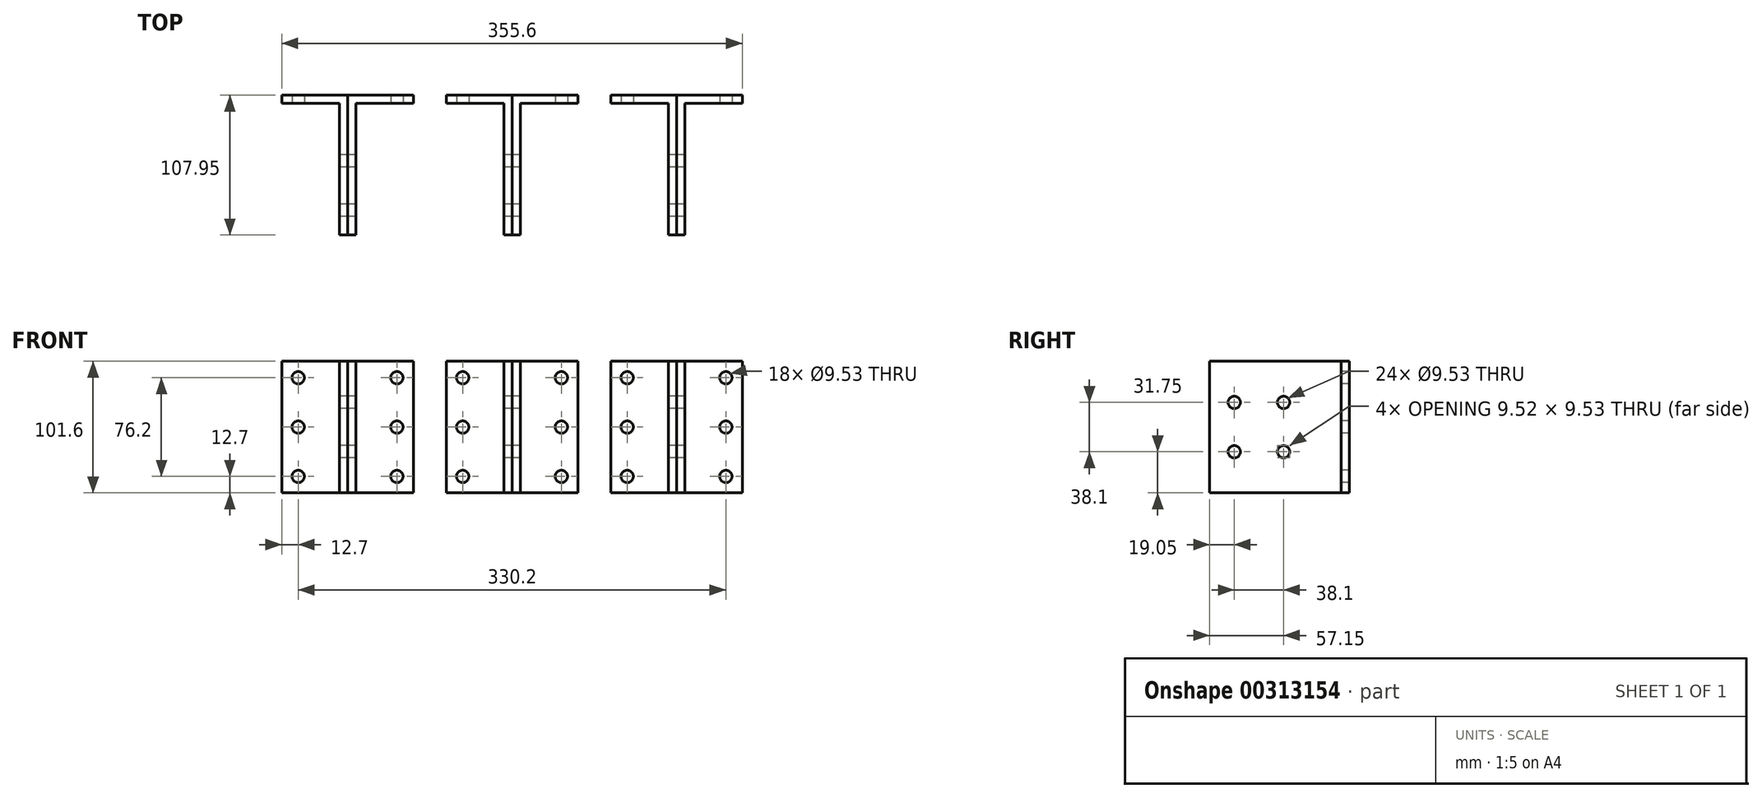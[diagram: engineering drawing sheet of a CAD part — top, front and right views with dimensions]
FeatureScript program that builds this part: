
annotation { "Feature Type Name" : "Feature", "Feature Type Description" : "" }
export const myFeature = defineFeature(function(context is Context, id is Id, definition is map)
    precondition{}
    {
        {
            var Q0;
            Q0=qCreatedBy(makeId("Top.planeOp"),FACE);
            var sketch = newSketch(context, id + "F0", { "sketchPlane" : qUnion([Q0])});
            skLineSegment(sketch, "E0", {"start": v(-44.45, 0) * mm, "end": v(0, 0) * mm});
            skLineSegment(sketch, "E1", {"start": v(0, 0) * mm, "end": v(0, -101.6) * mm});
            skLineSegment(sketch, "E2", {"start": v(0, -101.6) * mm, "end": v(6.35, -101.6) * mm});
            skLineSegment(sketch, "E3", {"start": v(6.35, -101.6) * mm, "end": v(6.35, 6.35) * mm});
            skLineSegment(sketch, "E4", {"start": v(6.35, 6.35) * mm, "end": v(-44.45, 6.35) * mm});
            skLineSegment(sketch, "E5", {"start": v(-44.45, 6.35) * mm, "end": v(-44.45, 0) * mm});
            skLineSegment(sketch, "E6.1.0.0", {"start": v(82.55, 0) * mm, "end": v(127, 0) * mm});
            skLineSegment(sketch, "E6.1.0.1", {"start": v(127, 0) * mm, "end": v(127, -101.6) * mm});
            skLineSegment(sketch, "E6.1.0.2", {"start": v(133.35, -101.6) * mm, "end": v(133.35, 6.35) * mm});
            skLineSegment(sketch, "E6.1.0.3", {"start": v(133.35, 6.35) * mm, "end": v(82.55, 6.35) * mm});
            skLineSegment(sketch, "E6.1.0.4", {"start": v(127, -101.6) * mm, "end": v(133.35, -101.6) * mm});
            skLineSegment(sketch, "E6.1.0.5", {"start": v(82.55, 6.35) * mm, "end": v(82.55, 0) * mm});
            skLineSegment(sketch, "E6.2.0.0", {"start": v(209.55, 0) * mm, "end": v(254, 0) * mm});
            skLineSegment(sketch, "E6.2.0.1", {"start": v(254, 0) * mm, "end": v(254, -101.6) * mm});
            skLineSegment(sketch, "E6.2.0.2", {"start": v(260.35, -101.6) * mm, "end": v(260.35, 6.35) * mm});
            skLineSegment(sketch, "E6.2.0.3", {"start": v(260.35, 6.35) * mm, "end": v(209.55, 6.35) * mm});
            skLineSegment(sketch, "E6.2.0.4", {"start": v(254, -101.6) * mm, "end": v(260.35, -101.6) * mm});
            skLineSegment(sketch, "E6.2.0.5", {"start": v(209.55, 6.35) * mm, "end": v(209.55, 0) * mm});
            skLineSegment(sketch, "E6.direction1", {"start": v(0, -101.6) * mm, "end": v(127, -101.6) * mm, "construction": true});
            skSolve(sketch);
        }
        {
            var Q0;
            Q0=qCreatedBy(makeId("Top.planeOp"),FACE);
            var sketch = newSketch(context, id + "F1", { "sketchPlane" : qUnion([Q0])});
            skLineSegment(sketch, "E7", {"start": v(6.35, 6.35) * mm, "end": v(6.35, -101.6) * mm});
            skLineSegment(sketch, "E8", {"start": v(6.35, -101.6) * mm, "end": v(12.7, -101.6) * mm});
            skLineSegment(sketch, "E9", {"start": v(12.7, -101.6) * mm, "end": v(12.7, 0) * mm});
            skLineSegment(sketch, "E10", {"start": v(12.7, 0) * mm, "end": v(57.15, 0) * mm});
            skLineSegment(sketch, "E11", {"start": v(6.35, 6.35) * mm, "end": v(57.15, 6.35) * mm});
            skLineSegment(sketch, "E12", {"start": v(57.15, 6.35) * mm, "end": v(57.15, 0) * mm});
            skLineSegment(sketch, "E13.1.0.0", {"start": v(133.35, 6.35) * mm, "end": v(133.35, -101.6) * mm});
            skLineSegment(sketch, "E13.1.0.1", {"start": v(139.7, -101.6) * mm, "end": v(139.7, 0) * mm});
            skLineSegment(sketch, "E13.1.0.2", {"start": v(139.7, 0) * mm, "end": v(184.15, 0) * mm});
            skLineSegment(sketch, "E13.1.0.3", {"start": v(133.35, 6.35) * mm, "end": v(184.15, 6.35) * mm});
            skLineSegment(sketch, "E13.1.0.4", {"start": v(133.35, -101.6) * mm, "end": v(139.7, -101.6) * mm});
            skLineSegment(sketch, "E13.1.0.5", {"start": v(184.15, 6.35) * mm, "end": v(184.15, 0) * mm});
            skLineSegment(sketch, "E13.2.0.0", {"start": v(260.35, 6.35) * mm, "end": v(260.35, -101.6) * mm});
            skLineSegment(sketch, "E13.2.0.1", {"start": v(266.7, -101.6) * mm, "end": v(266.7, 0) * mm});
            skLineSegment(sketch, "E13.2.0.2", {"start": v(266.7, 0) * mm, "end": v(311.15, 0) * mm});
            skLineSegment(sketch, "E13.2.0.3", {"start": v(260.35, 6.35) * mm, "end": v(311.15, 6.35) * mm});
            skLineSegment(sketch, "E13.2.0.4", {"start": v(260.35, -101.6) * mm, "end": v(266.7, -101.6) * mm});
            skLineSegment(sketch, "E13.2.0.5", {"start": v(311.15, 6.35) * mm, "end": v(311.15, 0) * mm});
            skLineSegment(sketch, "E13.direction1", {"start": v(6.35, -101.6) * mm, "end": v(133.35, -101.6) * mm, "construction": true});
            skSolve(sketch);
        }
        {
            var Q0;
            Q0 = qSketchRegion(id + "F0", true);
            var Q1;
            Q1 = qSketchRegion(id + "F1", true);
            extrude(context, id + "F2", {"entities" : qUnion([Q0, Q1]), "endBound" : BoundingType.SYMMETRIC, "depth" : 101.6 * mm});
        }
        {
            var Q0;
            Q0=makeQuery(id+"F2.opExtrude","SWEPT_FACE",FACE,{"disambiguationData":[OSD([sQuery(id+"F1.wireOp",EDGE,"E10")])]});
            var sketch = newSketch(context, id + "F3", { "sketchPlane" : qUnion([Q0])});
            skCircle(sketch, "E14", {"center": v(-31.75, 38.1) * mm, "radius": 4.76 * mm});
            skCircle(sketch, "E15.0.1.0", {"center": v(-31.75, 0) * mm, "radius": 4.76 * mm});
            skCircle(sketch, "E15.0.2.0", {"center": v(-31.75, -38.1) * mm, "radius": 4.76 * mm});
            skCircle(sketch, "E15.1.0.0", {"center": v(44.45, 38.1) * mm, "radius": 4.76 * mm});
            skCircle(sketch, "E15.1.1.0", {"center": v(44.45, 0) * mm, "radius": 4.76 * mm});
            skCircle(sketch, "E15.1.2.0", {"center": v(44.45, -38.1) * mm, "radius": 4.76 * mm});
            skLineSegment(sketch, "E15.direction1", {"start": v(-31.75, 38.1) * mm, "end": v(44.45, 38.1) * mm, "construction": true});
            skLineSegment(sketch, "E15.direction2", {"start": v(-31.75, 38.1) * mm, "end": v(-31.75, 0) * mm, "construction": true});
            skCircle(sketch, "E16.1.0.0", {"center": v(95.25, -38.1) * mm, "radius": 4.76 * mm});
            skCircle(sketch, "E16.1.0.1", {"center": v(171.45, 38.1) * mm, "radius": 4.76 * mm});
            skCircle(sketch, "E16.1.0.2", {"center": v(171.45, 0) * mm, "radius": 4.76 * mm});
            skCircle(sketch, "E16.1.0.3", {"center": v(171.45, -38.1) * mm, "radius": 4.76 * mm});
            skLineSegment(sketch, "E16.1.0.4", {"start": v(95.25, 38.1) * mm, "end": v(171.45, 38.1) * mm, "construction": true});
            skLineSegment(sketch, "E16.1.0.5", {"start": v(95.25, 38.1) * mm, "end": v(95.25, 0) * mm, "construction": true});
            skCircle(sketch, "E16.1.0.6", {"center": v(95.25, 38.1) * mm, "radius": 4.76 * mm});
            skCircle(sketch, "E16.1.0.7", {"center": v(95.25, 0) * mm, "radius": 4.76 * mm});
            skCircle(sketch, "E16.2.0.0", {"center": v(222.25, -38.1) * mm, "radius": 4.76 * mm});
            skCircle(sketch, "E16.2.0.1", {"center": v(298.45, 38.1) * mm, "radius": 4.76 * mm});
            skCircle(sketch, "E16.2.0.2", {"center": v(298.45, 0) * mm, "radius": 4.76 * mm});
            skCircle(sketch, "E16.2.0.3", {"center": v(298.45, -38.1) * mm, "radius": 4.76 * mm});
            skLineSegment(sketch, "E16.2.0.4", {"start": v(222.25, 38.1) * mm, "end": v(298.45, 38.1) * mm, "construction": true});
            skLineSegment(sketch, "E16.2.0.5", {"start": v(222.25, 38.1) * mm, "end": v(222.25, 0) * mm, "construction": true});
            skCircle(sketch, "E16.2.0.6", {"center": v(222.25, 38.1) * mm, "radius": 4.76 * mm});
            skCircle(sketch, "E16.2.0.7", {"center": v(222.25, 0) * mm, "radius": 4.76 * mm});
            skLineSegment(sketch, "E16.direction1", {"start": v(-31.75, -38.1) * mm, "end": v(95.25, -38.1) * mm, "construction": true});
            skSolve(sketch);
        }
        {
            var Q0;
            Q0 = qSketchRegion(id + "F3", true);
            extrude(context, id + "F4", {"entities" : qUnion([Q0]), "operationType" : NewBodyOperationType.REMOVE, "endBound" : BoundingType.THROUGH_ALL, "oppositeDirection" : true, "depth" : 25.4 * mm});
        }
        {
            var Q0;
            Q0=makeQuery(id+"F2.opExtrude","SWEPT_FACE",FACE,{"disambiguationData":[OSD([sQuery(id+"F0.wireOp",EDGE,"E1")])]});
            var sketch = newSketch(context, id + "F5", { "sketchPlane" : qUnion([Q0])});
            skCircle(sketch, "E17", {"center": v(82.55, 19.05) * mm, "radius": 4.76 * mm});
            skCircle(sketch, "E18.0.1.0", {"center": v(82.55, -19.05) * mm, "radius": 4.76 * mm});
            skCircle(sketch, "E18.1.0.0", {"center": v(44.45, 19.05) * mm, "radius": 4.76 * mm});
            skCircle(sketch, "E18.1.1.0", {"center": v(44.45, -19.05) * mm, "radius": 4.76 * mm});
            skLineSegment(sketch, "E18.direction1", {"start": v(82.55, 19.05) * mm, "end": v(44.45, 19.05) * mm, "construction": true});
            skLineSegment(sketch, "E18.direction2", {"start": v(82.55, 19.05) * mm, "end": v(82.55, -19.05) * mm, "construction": true});
            skPoint(sketch, "E19", {"position": v(82.55, 0) * mm});
            skSolve(sketch);
        }
        {
            var Q0;
            Q0 = qSketchRegion(id + "F5", true);
            extrude(context, id + "F6", {"entities" : qUnion([Q0]), "operationType" : NewBodyOperationType.REMOVE, "endBound" : BoundingType.THROUGH_ALL, "oppositeDirection" : true, "depth" : 25.4 * mm});
        }
    });
